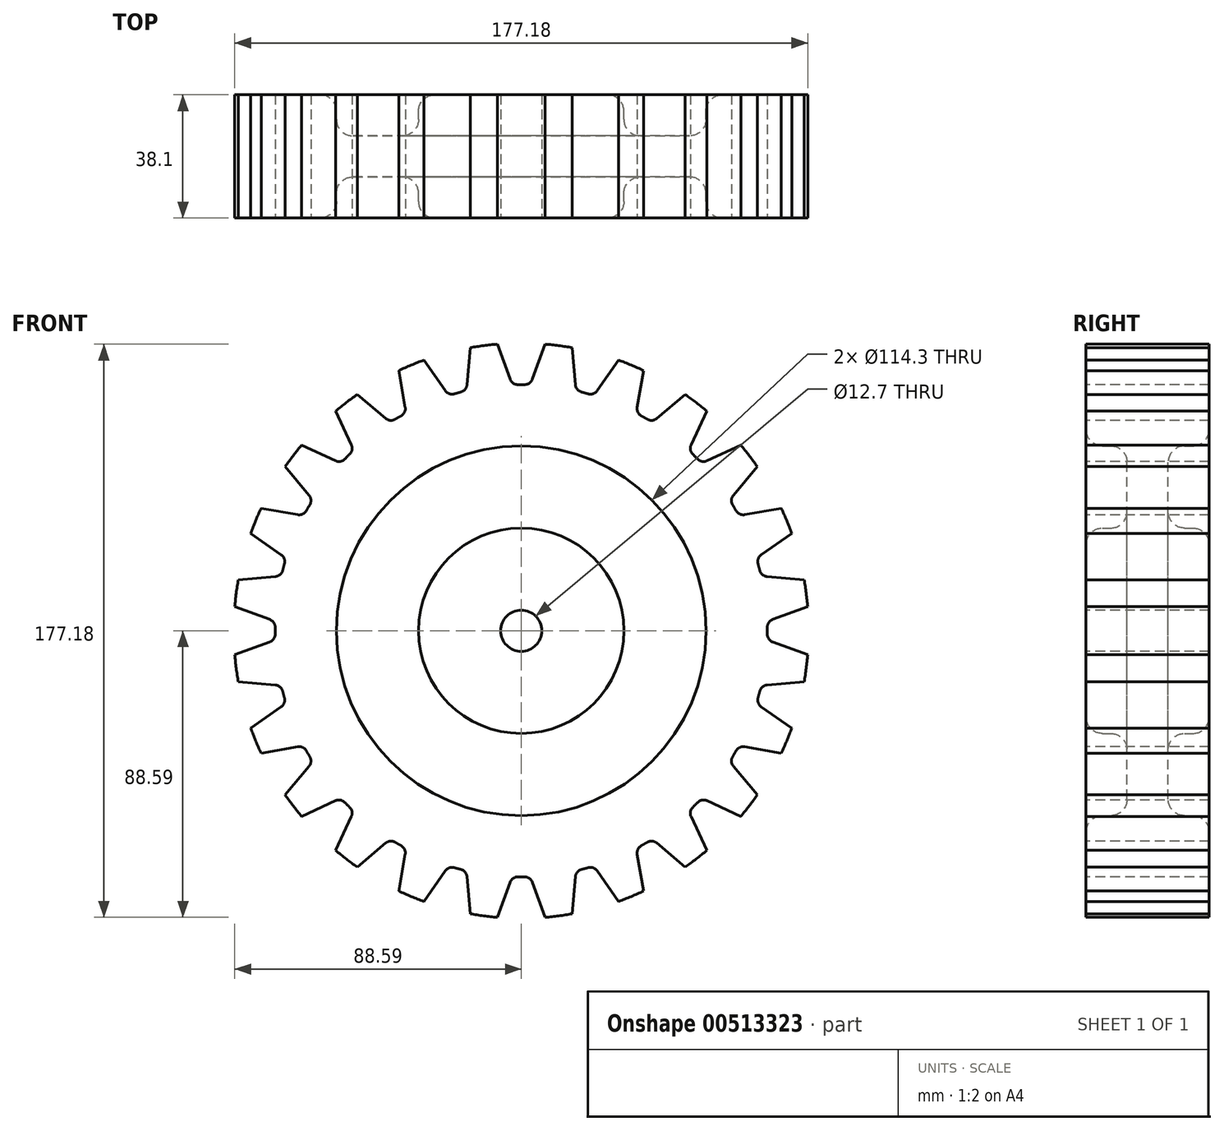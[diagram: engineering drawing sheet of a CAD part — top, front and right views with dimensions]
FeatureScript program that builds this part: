
annotation { "Feature Type Name" : "Feature", "Feature Type Description" : "" }
export const myFeature = defineFeature(function(context is Context, id is Id, definition is map)
    precondition{}
    {
        {
            var Q0;
            Q0=qCreatedBy(makeId("Right.planeOp"),FACE);
            var sketch = newSketch(context, id + "F0", { "sketchPlane" : qUnion([Q0])});
            skLineSegment(sketch, "E0.left", {"start": v(6.35, -12.7) * mm, "end": v(6.35, 12.7) * mm});
            skLineSegment(sketch, "E0.right", {"start": v(-6.35, -12.7) * mm, "end": v(-6.35, 12.7) * mm});
            skPoint(sketch, "E0.middle", {"position": v(0, 0) * mm});
            skLineSegment(sketch, "E1.bottom", {"start": v(19.05, 44.45) * mm, "end": v(-19.05, 44.45) * mm});
            skLineSegment(sketch, "E1.top", {"start": v(19.05, 12.7) * mm, "end": v(6.35, 12.7) * mm});
            skLineSegment(sketch, "E1.left", {"start": v(19.05, 44.45) * mm, "end": v(19.05, 12.7) * mm});
            skLineSegment(sketch, "E1.right", {"start": v(-19.05, 44.45) * mm, "end": v(-19.05, 12.7) * mm});
            skPoint(sketch, "E1.middle", {"position": v(0, 28.58) * mm});
            skLineSegment(sketch, "E2.bottom", {"start": v(19.05, -44.45) * mm, "end": v(-19.05, -44.45) * mm});
            skLineSegment(sketch, "E2.top", {"start": v(19.05, -12.7) * mm, "end": v(6.35, -12.7) * mm});
            skLineSegment(sketch, "E2.left", {"start": v(19.05, -44.45) * mm, "end": v(19.05, -12.7) * mm});
            skLineSegment(sketch, "E2.right", {"start": v(-19.05, -44.45) * mm, "end": v(-19.05, -12.7) * mm});
            skPoint(sketch, "E2.middle", {"position": v(0, -28.58) * mm});
            skLineSegment(sketch, "E3.trimOffspring", {"start": v(-6.35, 12.7) * mm, "end": v(-19.05, 12.7) * mm});
            skPoint(sketch, "E4.end.orphan", {"position": v(-6.35, 28.58) * mm});
            skPoint(sketch, "E4.start.orphan", {"position": v(-19.05, 28.58) * mm});
            skPoint(sketch, "E5.trimOffspring.end.orphan", {"position": v(19.05, 28.58) * mm});
            skPoint(sketch, "E6.orphan", {"position": v(6.35, 28.58) * mm});
            skLineSegment(sketch, "E7.trimOffspring", {"start": v(-6.35, -12.7) * mm, "end": v(-19.05, -12.7) * mm});
            skPoint(sketch, "E8.trimOffspring.end.orphan", {"position": v(19.05, -28.58) * mm});
            skPoint(sketch, "E9.orphan", {"position": v(6.35, -28.58) * mm});
            skPoint(sketch, "E10.orphan", {"position": v(-19.05, -28.58) * mm});
            skPoint(sketch, "E0.bottom.end.orphan", {"position": v(-6.35, -28.58) * mm});
            skSolve(sketch);
        }
        {
            var Q0;
            Q0=makeQuery(id+"F0.imprint","IMPRINT",FACE,{"disambiguationData":[TD([[makeQuery(id+"F0.imprint","IMPRINT",EDGE,{"derivedFrom":sQuery(id+"F0.wireOp",EDGE,"E0.left")}),1.0]])]});
            var Q1;
            Q1=sQuery(id+"F0.wireOp",EDGE,"E1.bottom");
            revolve(context, id + "F1", {"entities" : qUnion([Q0]), "axis" : qUnion([Q1]), "revolveType" : RevolveType.FULL});
        }
        {
            var Q0;
            Q0=makeQuery(id+"F1.opRevolve","SWEPT_FACE",FACE,{"disambiguationData":[OSD([sQuery(id+"F0.wireOp",EDGE,"E1.right")])]});
            var sketch = newSketch(context, id + "F2", { "sketchPlane" : qUnion([Q0])});
            skCircle(sketch, "E11", {"center": v(0, 44.45) * mm, "radius": 6.35 * mm});
            skSolve(sketch);
        }
        {
            var Q0;
            Q0 = qSketchRegion(id + "F2", true);
            extrude(context, id + "F3", {"entities" : qUnion([Q0]), "operationType" : NewBodyOperationType.REMOVE, "oppositeDirection" : true, "depth" : 38.1 * mm});
        }
        {
            var Q0;
            Q0=makeQuery(id+"F1.opRevolve","SWEPT_EDGE",EDGE,{"disambiguationData":[OSD([sQuery(id+"F0.wireOp",EDGE,"E0.right"),sQuery(id+"F0.wireOp",EDGE,"E7.trimOffspring")])]});
            var Q1;
            Q1=makeQuery(id+"F1.opRevolve","SWEPT_EDGE",EDGE,{"disambiguationData":[OSD([sQuery(id+"F0.wireOp",EDGE,"E2.right"),sQuery(id+"F0.wireOp",EDGE,"E7.trimOffspring")])]});
            var Q2;
            Q2=makeQuery(id+"F1.opRevolve","SWEPT_EDGE",EDGE,{"disambiguationData":[OSD([sQuery(id+"F0.wireOp",EDGE,"E0.right"),sQuery(id+"F0.wireOp",EDGE,"E3.trimOffspring")])]});
            var Q3;
            Q3=makeQuery(id+"F1.opRevolve","SWEPT_EDGE",EDGE,{"disambiguationData":[OSD([sQuery(id+"F0.wireOp",EDGE,"E1.right"),sQuery(id+"F0.wireOp",EDGE,"E3.trimOffspring")])]});
            var Q4;
            Q4=makeQuery(id+"F1.opRevolve","SWEPT_EDGE",EDGE,{"disambiguationData":[OSD([sQuery(id+"F0.wireOp",EDGE,"E2.top"),sQuery(id+"F0.wireOp",EDGE,"E2.left")])]});
            var Q5;
            Q5=makeQuery(id+"F1.opRevolve","SWEPT_EDGE",EDGE,{"disambiguationData":[OSD([sQuery(id+"F0.wireOp",EDGE,"E0.left"),sQuery(id+"F0.wireOp",EDGE,"E2.top")])]});
            var Q6;
            Q6=makeQuery(id+"F1.opRevolve","SWEPT_EDGE",EDGE,{"disambiguationData":[OSD([sQuery(id+"F0.wireOp",EDGE,"E0.left"),sQuery(id+"F0.wireOp",EDGE,"E1.top")])]});
            var Q7;
            Q7=makeQuery(id+"F1.opRevolve","SWEPT_EDGE",EDGE,{"disambiguationData":[OSD([sQuery(id+"F0.wireOp",EDGE,"E1.top"),sQuery(id+"F0.wireOp",EDGE,"E1.left")])]});
            fillet(context, id + "F4", {"entities" : qUnion([Q0, Q1, Q2, Q3, Q4, Q5, Q6, Q7]), "radius" : 5.08 * mm, "tangentPropagation" : true, "allowEdgeOverflow" : false});
        }
        {
            var Q0;
            Q0=qCreatedBy(makeId("Front.planeOp"),FACE);
            var sketch = newSketch(context, id + "F5", { "sketchPlane" : qUnion([Q0])});
            skArc(sketch, "E12", {"start": v(1.06, 120.55) * mm, "mid": v(0, 120.56) * mm, "end": v(-1.06, 120.55) * mm});
            skLineSegment(sketch, "E13", {"start": v(0, 44.36) * mm, "end": v(0, 176.37) * mm, "construction": true});
            skLineSegment(sketch, "E14", {"start": v(3.48, 122.22) * mm, "end": v(7.43, 133.07) * mm});
            skLineSegment(sketch, "E15.MirrorCS", {"start": v(-3.48, 122.22) * mm, "end": v(-7.43, 133.07) * mm});
            skArc(sketch, "E16", {"start": v(7.43, 133.07) * mm, "mid": v(0, 133.38) * mm, "end": v(-7.43, 133.07) * mm});
            skPoint(sketch, "E17.visualSharp", {"position": v(-2.85, 120.5) * mm});
            skArc(sketch, "E17.filletArc", {"start": v(-3.48, 122.22) * mm, "mid": v(-2.53, 121) * mm, "end": v(-1.06, 120.55) * mm});
            skPoint(sketch, "E18.visualSharp", {"position": v(2.85, 120.5) * mm});
            skArc(sketch, "E18.filletArc", {"start": v(1.06, 120.55) * mm, "mid": v(2.53, 121) * mm, "end": v(3.48, 122.22) * mm});
            skSolve(sketch);
        }
        {
            var Q0;
            Q0 = qSketchRegion(id + "F5", true);
            extrude(context, id + "F6", {"entities" : qUnion([Q0]), "operationType" : NewBodyOperationType.REMOVE, "endBound" : BoundingType.SYMMETRIC, "oppositeDirection" : true, "depth" : 38.1 * mm});
        }
        {
            var Q0;
            Q0=makeQuery(id+"F6.boolean.opBoolean","COPY",FACE,{"derivedFrom":makeQuery(id+"F6.opExtrude","SWEPT_FACE",FACE,{"disambiguationData":[OSD([sQuery(id+"F5.wireOp",EDGE,"E15.MirrorCS")])]})});
            var Q1;
            Q1=makeQuery(id+"F6.boolean.opBoolean","COPY",FACE,{"derivedFrom":makeQuery(id+"F6.opExtrude","SWEPT_FACE",FACE,{"disambiguationData":[OSD([sQuery(id+"F5.wireOp",EDGE,"E17.filletArc")])]})});
            var Q2;
            Q2=makeQuery(id+"F6.boolean.opBoolean","COPY",FACE,{"derivedFrom":makeQuery(id+"F6.opExtrude","SWEPT_FACE",FACE,{"disambiguationData":[OSD([sQuery(id+"F5.wireOp",EDGE,"E12")])]})});
            var Q3;
            Q3=makeQuery(id+"F6.boolean.opBoolean","COPY",FACE,{"derivedFrom":makeQuery(id+"F6.opExtrude","SWEPT_FACE",FACE,{"disambiguationData":[OSD([sQuery(id+"F5.wireOp",EDGE,"E18.filletArc")])]})});
            var Q4;
            Q4=makeQuery(id+"F6.boolean.opBoolean","COPY",FACE,{"derivedFrom":makeQuery(id+"F6.opExtrude","SWEPT_FACE",FACE,{"disambiguationData":[OSD([sQuery(id+"F5.wireOp",EDGE,"E14")])]})});
            var Q5;
            Q5=makeQuery(id+"F1.opRevolve","SWEPT_FACE",FACE,{"disambiguationData":[OSD([sQuery(id+"F0.wireOp",EDGE,"E2.bottom")])]});
            circularPattern(context, id + "F7", {"patternType" : PatternType.FACE, "faces" : qUnion([Q0, Q1, Q2, Q3, Q4]), "axis" : qUnion([Q5]), "angle" : 360 * degree, "instanceCount" : 24, "equalSpace" : true});
        }
    });
